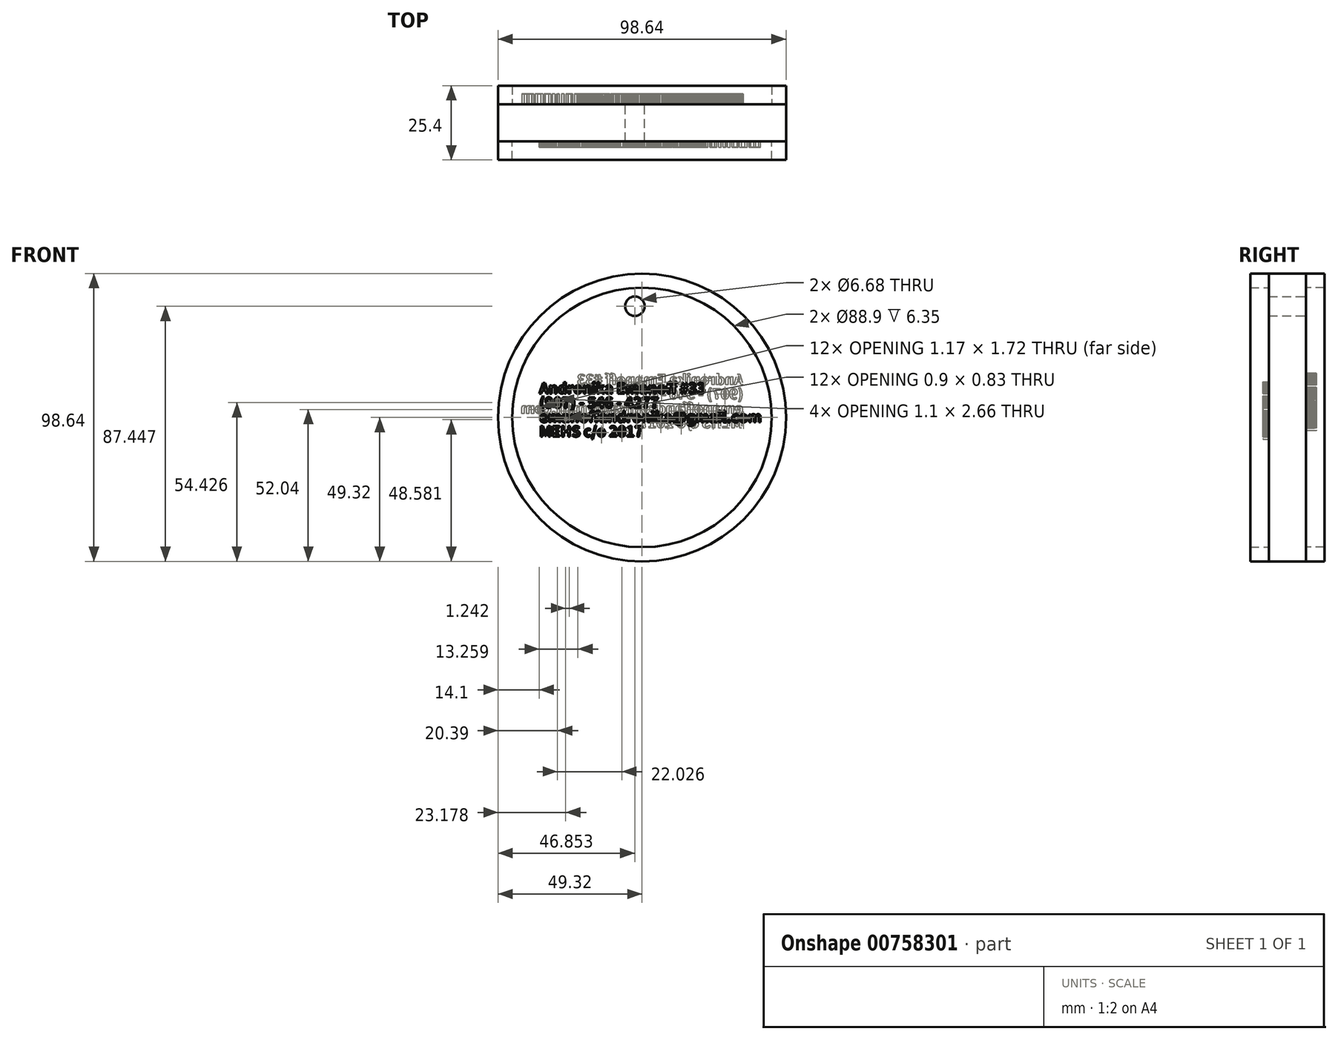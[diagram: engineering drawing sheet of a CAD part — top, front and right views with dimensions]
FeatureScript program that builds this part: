
annotation { "Feature Type Name" : "Feature", "Feature Type Description" : "" }
export const myFeature = defineFeature(function(context is Context, id is Id, definition is map)
    precondition{}
    {
        {
            var Q0;
            Q0=qCreatedBy(makeId("Front.planeOp"),FACE);
            var sketch = newSketch(context, id + "F0", { "sketchPlane" : qUnion([Q0])});
            skCircle(sketch, "E0", {"center": v(0, 0) * mm, "radius": 49.32 * mm});
            skSolve(sketch);
        }
        {
            var Q0;
            Q0=makeQuery(id+"F0.imprint","IMPRINT",FACE,{"disambiguationData":[TD([[makeQuery(id+"F0.imprint","IMPRINT",EDGE,{"derivedFrom":sQuery(id+"F0.wireOp",EDGE,"E0")}),1.0]])]});
            var sketch = newSketch(context, id + "F1", { "sketchPlane" : qUnion([Q0])});
            skSolve(sketch);
        }
        {
            var Q0;
            Q0 = qSketchRegion(id + "F1", true);
            var Q1;
            Q1=makeQuery(id+"F0.imprint","IMPRINT",FACE,{"disambiguationData":[TD([[makeQuery(id+"F0.imprint","IMPRINT",EDGE,{"derivedFrom":sQuery(id+"F0.wireOp",EDGE,"E0")}),1.0]])]});
            var Q2;
            Q2=makeQuery(id+"F1.imprint","IMPRINT",FACE,{"disambiguationData":[TD([[makeQuery(id+"F1.imprint","IMPRINT",EDGE,{"derivedFrom":makeQuery(id+"F0.imprint","IMPRINT",EDGE,{"derivedFrom":sQuery(id+"F0.wireOp",EDGE,"E0")})}),1.0]])]});
            extrude(context, id + "F2", {"entities" : qUnion([Q0, Q1, Q2]), "depth" : 12.7 * mm, "offsetDistance" : 25.4 * mm});
        }
        {
            var Q0;
            {var subQ0=sQuery(id+"F0.wireOp",EDGE,"E0");Q0=makeQuery(id+"F2.opExtrude","CAP_FACE",FACE,{"disambiguationData":[OSD([subQ0]),TDD([makeQuery(id+"F0.imprint","IMPRINT",EDGE,{"derivedFrom":subQ0})])],"isStart":false});}
            var sketch = newSketch(context, id + "F3", { "sketchPlane" : qUnion([Q0])});
            skText(sketch, "E1", { "text": "Andronika Emanoff #33\n(907) - 546 - 4277\<email>\nMEHS c/o 2017", "fontName": "NotoSansCJKtc-Bold.otf"});
            const initialGuessF3  = {"E1": [-0.03515, 0.00821, 1, 0, 0.00355]};
            skSetInitialGuess(sketch, initialGuessF3);
            skSolve(sketch);
        }
        {
            var Q0;
            Q0=makeQuery(id+"F3.imprint","IMPRINT",FACE,{"disambiguationData":[TD([[makeQuery(id+"F3.imprint","IMPRINT",EDGE,{"derivedFrom":sQuery(id+"F3.wireOp",EDGE,"E1.sketch_text.stroke-6")}),-1.0]])]});
            var sketch = newSketch(context, id + "F4", { "sketchPlane" : qUnion([Q0])});
            skSolve(sketch);
        }
        {
            var Q0;
            Q0=qCreatedBy(makeId("Front.planeOp"),FACE);
            var sketch = newSketch(context, id + "F5", { "sketchPlane" : qUnion([Q0])});
            skSolve(sketch);
        }
        {
            var Q0;
            Q0 = qSketchRegion(id + "F5", true);
            var Q1;
            Q1 = qSketchRegion(id + "F3", true);
            extrude(context, id + "F6", {"entities" : qUnion([Q0, Q1]), "depth" : 2.03 * mm, "offsetDistance" : 25.4 * mm});
        }
        {
            var Q0;
            {var subQ0=sQuery(id+"F0.wireOp",EDGE,"E0");Q0=makeQuery(id+"F2.opExtrude","CAP_FACE",FACE,{"disambiguationData":[OSD([subQ0]),TDD([makeQuery(id+"F0.imprint","IMPRINT",EDGE,{"derivedFrom":subQ0})])],"isStart":true});}
            var sketch = newSketch(context, id + "F7", { "sketchPlane" : qUnion([Q0])});
            skText(sketch, "E2", { "text": "Andronika Emanoff #33\n(907) - 546 - 4277\<email>\nMEHS c/o 2017", "fontName": "NotoSansCJKtc-Bold.otf"});
            const initialGuessF7  = {"E2": [-0.03464, 0.0112, 1, 0, 0.00355]};
            skSetInitialGuess(sketch, initialGuessF7);
            skSolve(sketch);
        }
        {
            var Q0;
            Q0=makeQuery(id+"F7.imprint","IMPRINT",FACE,{"disambiguationData":[TD([[makeQuery(id+"F7.imprint","IMPRINT",EDGE,{"derivedFrom":sQuery(id+"F7.wireOp",EDGE,"E2.sketch_text.stroke-6")}),-1.0]])]});
            var sketch = newSketch(context, id + "F8", { "sketchPlane" : qUnion([Q0])});
            skSolve(sketch);
        }
        {
            var Q0;
            Q0 = qSketchRegion(id + "F8", true);
            var Q1;
            Q1 = qSketchRegion(id + "F7", true);
            extrude(context, id + "F9", {"entities" : qUnion([Q0, Q1]), "depth" : 3.56 * mm, "offsetDistance" : 25.4 * mm});
        }
        {
            var Q0;
            Q0=makeQuery(id+"F8.imprint","IMPRINT",FACE,{"disambiguationData":[TD([[makeQuery(id+"F8.imprint","IMPRINT",EDGE,{"derivedFrom":makeQuery(id+"F7.imprint","IMPRINT",EDGE,{"derivedFrom":sQuery(id+"F7.wireOp",EDGE,"E2.sketch_text.stroke-6")})}),-1.0]])]});
            var sketch = newSketch(context, id + "F10", { "sketchPlane" : qUnion([Q0])});
            skCircle(sketch, "E3", {"center": v(2.47, 38.13) * mm, "radius": 3.34 * mm});
            skSolve(sketch);
        }
        {
            var Q0;
            Q0 = qSketchRegion(id + "F10", true);
            extrude(context, id + "F11", {"entities" : qUnion([Q0]), "operationType" : NewBodyOperationType.REMOVE, "oppositeDirection" : true, "depth" : 25.4 * mm, "offsetDistance" : 25.4 * mm});
        }
        {
            var Q0;
            Q0=makeQuery(id+"F4.imprint","IMPRINT",FACE,{"disambiguationData":[TD([[makeQuery(id+"F4.imprint","IMPRINT",EDGE,{"derivedFrom":makeQuery(id+"F3.imprint","IMPRINT",EDGE,{"derivedFrom":sQuery(id+"F3.wireOp",EDGE,"E1.sketch_text.stroke-6")})}),-1.0]])]});
            var sketch = newSketch(context, id + "F12", { "sketchPlane" : qUnion([Q0])});
            skCircle(sketch, "E4", {"center": v(0, 0) * mm, "radius": 44.45 * mm});
            skSolve(sketch);
        }
        {
            var Q0;
            Q0=makeQuery(id+"F8.imprint","IMPRINT",FACE,{"disambiguationData":[TD([[makeQuery(id+"F8.imprint","IMPRINT",EDGE,{"derivedFrom":makeQuery(id+"F7.imprint","IMPRINT",EDGE,{"derivedFrom":sQuery(id+"F7.wireOp",EDGE,"E2.sketch_text.stroke-6")})}),-1.0]])]});
            var sketch = newSketch(context, id + "F13", { "sketchPlane" : qUnion([Q0])});
            skCircle(sketch, "E5", {"center": v(0, 0) * mm, "radius": 44.45 * mm});
            skSolve(sketch);
        }
        {
            var Q0;
            Q0=makeQuery(id+"F13.imprint","IMPRINT",FACE,{"disambiguationData":[TD([[makeQuery(id+"F13.imprint","IMPRINT",EDGE,{"derivedFrom":sQuery(id+"F13.wireOp",EDGE,"E5")}),-1.0]])]});
            extrude(context, id + "F14", {"entities" : qUnion([Q0]), "depth" : 6.35 * mm, "offsetDistance" : 25.4 * mm});
        }
        {
            var Q0;
            Q0=makeQuery(id+"F12.imprint","IMPRINT",FACE,{"disambiguationData":[TD([[makeQuery(id+"F12.imprint","IMPRINT",EDGE,{"derivedFrom":sQuery(id+"F12.wireOp",EDGE,"E4")}),-1.0]])]});
            extrude(context, id + "F15", {"entities" : qUnion([Q0]), "depth" : 6.35 * mm, "offsetDistance" : 25.4 * mm});
        }
    });
